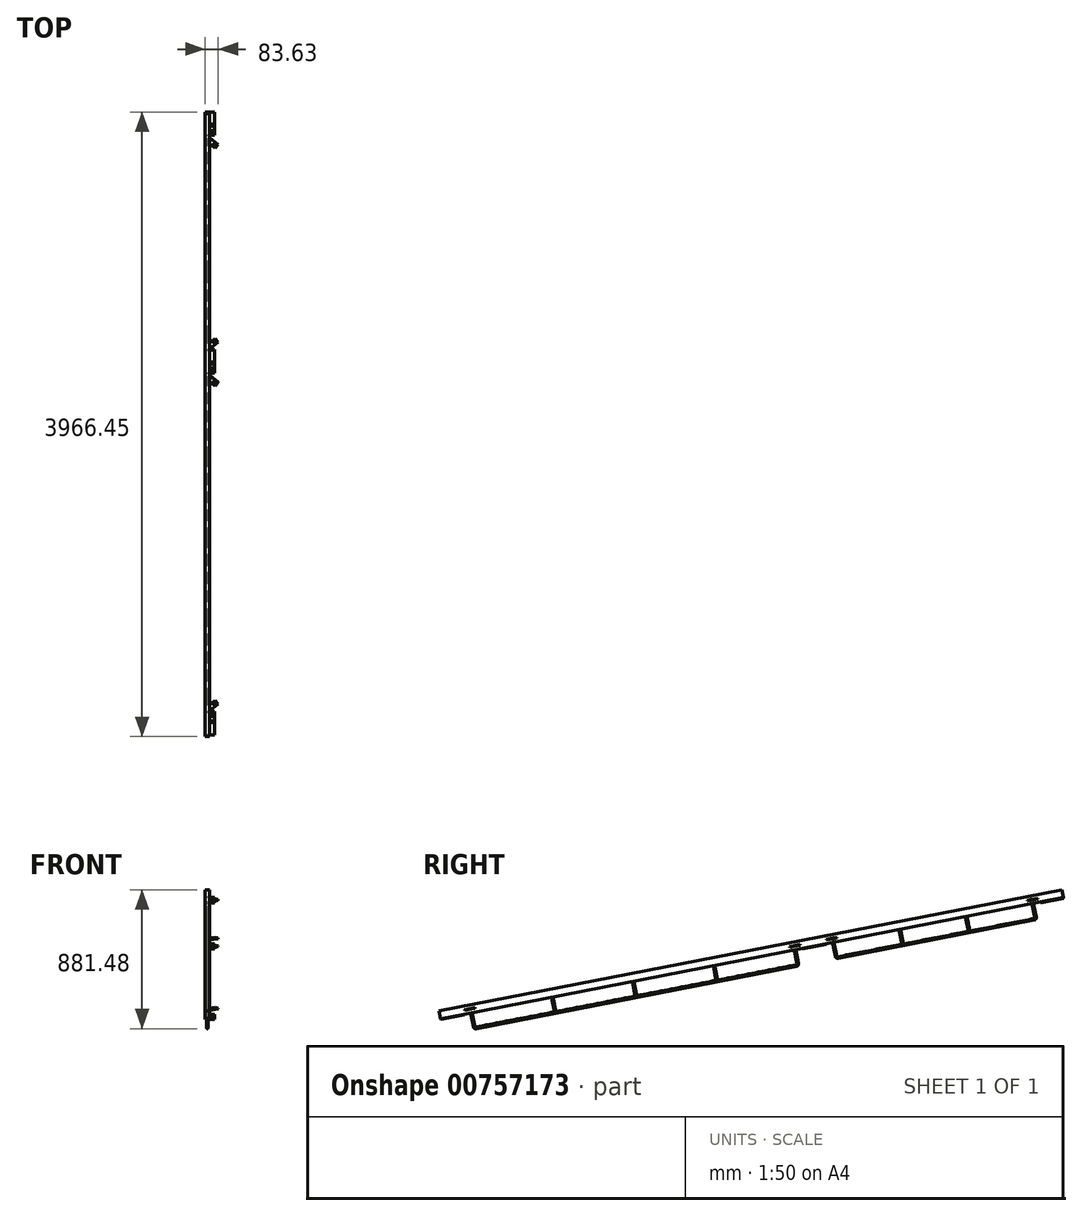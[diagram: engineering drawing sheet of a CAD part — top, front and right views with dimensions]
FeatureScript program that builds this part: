
annotation { "Feature Type Name" : "Feature", "Feature Type Description" : "" }
export const myFeature = defineFeature(function(context is Context, id is Id, definition is map)
    precondition{}
    {
        {
            var Q0;
            Q0=qCreatedBy(makeId("Top.planeOp"),FACE);
            var sketch = newSketch(context, id + "F0", { "sketchPlane" : qUnion([Q0])});
            skPoint(sketch, "E0", {"position": v(0, 0) * mm});
            skPoint(sketch, "E1", {"position": v(28.11, 0) * mm});
            skLineSegment(sketch, "E2", {"start": v(0, 0) * mm, "end": v(28.11, 0) * mm});
            skSolve(sketch);
        }
        {
            var Q0;
            Q0=qCreatedBy(makeId("Top.planeOp"),FACE);
            var Q1;
            Q1=sQuery(id+"F0.wireOp",EDGE,"E2");
            cPlane(context, id + "F1", {"entities" : qUnion([Q0, Q1]), "cplaneType" : CPlaneType.LINE_ANGLE, "offset" : 25 * mm, "angle" : 11 * degree, "width" : 150 * mm, "height" : 150 * mm});
        }
        {
            var Q0;
            Q0=qCreatedBy(id+"F1.planeOp",FACE);
            var Q1;
            Q1=sQuery(id+"F0.wireOp",EDGE,"E2");
            cPlane(context, id + "F2", {"entities" : qUnion([Q0, Q1]), "cplaneType" : CPlaneType.LINE_ANGLE, "offset" : 25 * mm, "angle" : 90 * degree, "width" : 150 * mm, "height" : 150 * mm});
        }
        {
            var Q0;
            Q0=qCreatedBy(id+"F2.planeOp",FACE);
            var sketch = newSketch(context, id + "F3", { "sketchPlane" : qUnion([Q0])});
            skLineSegment(sketch, "E3.bottom", {"start": v(15, -25) * mm, "end": v(-15, -25) * mm});
            skLineSegment(sketch, "E3.top", {"start": v(15, 25) * mm, "end": v(-15, 25) * mm});
            skLineSegment(sketch, "E3.left", {"start": v(15, -25) * mm, "end": v(15, 25) * mm});
            skLineSegment(sketch, "E3.right", {"start": v(-15, -25) * mm, "end": v(-15, 25) * mm});
            skPoint(sketch, "E3.middle", {"position": v(0, 0) * mm});
            skLineSegment(sketch, "E4.bottom", {"start": v(14, -24) * mm, "end": v(-14, -24) * mm});
            skLineSegment(sketch, "E4.top", {"start": v(14, 24) * mm, "end": v(-14, 24) * mm});
            skLineSegment(sketch, "E4.left", {"start": v(14, -24) * mm, "end": v(14, 24) * mm});
            skLineSegment(sketch, "E4.right", {"start": v(-14, -24) * mm, "end": v(-14, 24) * mm});
            skSolve(sketch);
        }
        {
            var Q0;
            Q0 = qSketchRegion(id + "F3", true);
            extrude(context, id + "F4", {"entities" : qUnion([Q0]), "depth" : 30 * mm, "offsetDistance" : 25 * mm, "hasSecondDirection" : true, "secondDirectionOppositeDirection" : true, "secondDirectionDepth" : 4000 * mm});
        }
        {
            var Q0;
            Q0=makeQuery(id+"F4.opExtrude","SWEPT_FACE",FACE,{"disambiguationData":[OSD([sQuery(id+"F3.wireOp",EDGE,"E3.bottom")])]});
            var sketch = newSketch(context, id + "F5", { "sketchPlane" : qUnion([Q0])});
            skLineSegment(sketch, "E5.0", {"start": v(45, -4000) * mm, "end": v(135, -4000) * mm});
            skLineSegment(sketch, "E6.0", {"start": v(-15, -4000) * mm, "end": v(45, -4000) * mm});
            skLineSegment(sketch, "E7.0", {"start": v(-15, -4000) * mm, "end": v(-15, -3850) * mm});
            skLineSegment(sketch, "E8.0", {"start": v(-15, -3850) * mm, "end": v(45, -3850) * mm});
            skLineSegment(sketch, "E9.0", {"start": v(45, -3940) * mm, "end": v(45, -3850) * mm});
            skLineSegment(sketch, "E10.0", {"start": v(45, -3940) * mm, "end": v(135, -3940) * mm});
            skLineSegment(sketch, "E11.0", {"start": v(135, -4000) * mm, "end": v(135, -3940) * mm});
            skCircle(sketch, "E12.0", {"center": v(70, -3955) * mm, "radius": 6 * mm});
            skCircle(sketch, "E13.0", {"center": v(110, -3955) * mm, "radius": 6 * mm});
            skCircle(sketch, "E14.0", {"center": v(30, -3915) * mm, "radius": 6 * mm});
            skCircle(sketch, "E15.0", {"center": v(30, -3875) * mm, "radius": 6 * mm});
            skLineSegment(sketch, "E16", {"start": v(45, -3940) * mm, "end": v(45, -4000) * mm});
            skSolve(sketch);
        }
        {
            var Q0;
            {var subQ0=sQuery(id+"F5.wireOp",EDGE,"E9.0");Q0=makeQuery(id+"F5.imprint","IMPRINT",FACE,{"disambiguationData":[TD([[makeQuery(id+"F5.imprint","IMPRINT",EDGE,{"derivedFrom":subQ0}),1.0]])]});}
            var Q1;
            {var subQ4=sQuery(id+"F5.wireOp",EDGE,"E7.0");Q1=makeQuery(id+"F5.imprint","IMPRINT",FACE,{"disambiguationData":[TD([[makeQuery(id+"F5.imprint","IMPRINT",EDGE,{"derivedFrom":subQ4}),1.0]])]});}
            extrude(context, id + "F6", {"entities" : qUnion([Q0, Q1]), "operationType" : NewBodyOperationType.ADD, "depth" : 5 * mm, "offsetDistance" : 25 * mm});
        }
        {
            var Q0;
            Q0=makeQuery(id+"F4.opExtrude","SWEPT_FACE",FACE,{"disambiguationData":[OSD([sQuery(id+"F3.wireOp",EDGE,"E3.bottom")])]});
            var sketch = newSketch(context, id + "F7", { "sketchPlane" : qUnion([Q0])});
            skLineSegment(sketch, "E17.0", {"start": v(45, -2401.65) * mm, "end": v(45, -2311.65) * mm});
            skLineSegment(sketch, "E18.0", {"start": v(-15, -2311.65) * mm, "end": v(45, -2311.65) * mm});
            skLineSegment(sketch, "E19.0", {"start": v(-15, -2461.65) * mm, "end": v(135, -2461.65) * mm});
            skLineSegment(sketch, "E20.0", {"start": v(135, -2461.65) * mm, "end": v(135, -2401.65) * mm});
            skLineSegment(sketch, "E21.0", {"start": v(45, -2401.65) * mm, "end": v(135, -2401.65) * mm});
            skLineSegment(sketch, "E22", {"start": v(-15, -2461.65) * mm, "end": v(-15, -2311.65) * mm});
            skLineSegment(sketch, "E23", {"start": v(45, -2401.65) * mm, "end": v(45, -2461.65) * mm});
            skCircle(sketch, "E24.0", {"center": v(30, -2376.65) * mm, "radius": 6 * mm});
            skCircle(sketch, "E25.0", {"center": v(30, -2336.65) * mm, "radius": 6 * mm});
            skSolve(sketch);
        }
        {
            var Q0;
            {var subQ0=sQuery(id+"F7.wireOp",EDGE,"E22");Q0=makeQuery(id+"F7.imprint","IMPRINT",FACE,{"disambiguationData":[TD([[makeQuery(id+"F7.imprint","IMPRINT",EDGE,{"derivedFrom":subQ0}),1.0]])]});}
            var Q1;
            {var subQ7=sQuery(id+"F7.wireOp",EDGE,"E17.0");Q1=makeQuery(id+"F7.imprint","IMPRINT",FACE,{"disambiguationData":[TD([[makeQuery(id+"F7.imprint","IMPRINT",EDGE,{"derivedFrom":subQ7}),1.0]])]});}
            extrude(context, id + "F8", {"entities" : qUnion([Q0, Q1]), "operationType" : NewBodyOperationType.ADD, "depth" : 5 * mm, "offsetDistance" : 25 * mm});
        }
        {
            var Q0;
            {var subQ3=sQuery(id+"F3.wireOp",EDGE,"E3.bottom");var subQ4=sQuery(id+"F7.wireOp",EDGE,"E18.0");Q0=makeQuery(id+"F8.boolean.opBoolean","SPLIT",FACE,{"disambiguationData":[TD([makeQuery(id+"F8.opExtrude","SWEPT_FACE",FACE,{"disambiguationData":[OSD([subQ4])]})])],"derivedFrom":makeQuery(id+"F4.opExtrude","SWEPT_FACE",FACE,{"disambiguationData":[OSD([subQ3])]})});}
            var sketch = newSketch(context, id + "F9", { "sketchPlane" : qUnion([Q0])});
            skLineSegment(sketch, "E26.0", {"start": v(-15, -120.03) * mm, "end": v(45, -120.03) * mm});
            skLineSegment(sketch, "E27.0", {"start": v(45, -30.03) * mm, "end": v(45, -120.03) * mm});
            skCircle(sketch, "E28.0", {"center": v(30, -95.03) * mm, "radius": 6 * mm});
            skCircle(sketch, "E29.0", {"center": v(30, -55.03) * mm, "radius": 6 * mm});
            skLineSegment(sketch, "E30.0", {"start": v(45, -30.03) * mm, "end": v(135, -30.03) * mm});
            skLineSegment(sketch, "E31.0", {"start": v(-15, 29) * mm, "end": v(135, 29) * mm});
            skLineSegment(sketch, "E32", {"start": v(-15, -120.03) * mm, "end": v(-15, 29) * mm});
            skLineSegment(sketch, "E33", {"start": v(45, -30.03) * mm, "end": v(45, 30) * mm});
            skSolve(sketch);
        }
        {
            var Q0;
            Q0 = qSketchRegion(id + "F9", true);
            extrude(context, id + "F10", {"entities" : qUnion([Q0]), "operationType" : NewBodyOperationType.ADD, "depth" : 4.8 * mm, "offsetDistance" : 25 * mm});
        }
        {
            var Q0;
            Q0=qCreatedBy(id+"F1.planeOp",FACE);
            var sketch = newSketch(context, id + "F11", { "sketchPlane" : qUnion([Q0])});
            skLineSegment(sketch, "E34.0", {"start": v(15, -3850) * mm, "end": v(45, -3850) * mm});
            skLineSegment(sketch, "E35", {"start": v(15, -3850) * mm, "end": v(15, -3840) * mm});
            skLineSegment(sketch, "E36", {"start": v(41, -1985.01) * mm, "end": v(15.07, -1985.01) * mm});
            skLineSegment(sketch, "E37.MirrorCS", {"start": v(15, -3840) * mm, "end": v(68.63, -3795) * mm});
            skLineSegment(sketch, "E38.MirrorCS", {"start": v(68.63, -3795) * mm, "end": v(49.34, -3772.03) * mm});
            skLineSegment(sketch, "E39.MirrorCS", {"start": v(49.34, -3772.03) * mm, "end": v(14.87, -3800.95) * mm});
            skCircle(sketch, "E40.MirrorC", {"center": v(43.27, -3796.7) * mm, "radius": 6 * mm});
            skLineSegment(sketch, "E41.MirrorCS", {"start": v(43.27, -3796.7) * mm, "end": v(58.99, -3783.52) * mm, "construction": true});
            skLineSegment(sketch, "E42", {"start": v(15, -3840) * mm, "end": v(14.87, -3800.95) * mm});
            skLineSegment(sketch, "E43.MirrorCS", {"start": v(15, -130.03) * mm, "end": v(68.63, -175.02) * mm});
            skCircle(sketch, "E44.MirrorC", {"center": v(43.27, -173.32) * mm, "radius": 6 * mm});
            skLineSegment(sketch, "E45.MirrorCS", {"start": v(43.27, -173.32) * mm, "end": v(58.99, -186.5) * mm, "construction": true});
            skLineSegment(sketch, "E46.MirrorCS", {"start": v(68.63, -175.02) * mm, "end": v(49.34, -198) * mm});
            skLineSegment(sketch, "E47.MirrorCS", {"start": v(49.34, -198) * mm, "end": v(14.87, -169.08) * mm});
            skLineSegment(sketch, "E48.MirrorCS", {"start": v(15, -130.03) * mm, "end": v(14.87, -169.08) * mm});
            skPoint(sketch, "E49.0", {"position": v(30, -2311.65) * mm});
            skLineSegment(sketch, "E50.0", {"start": v(15, -2311.65) * mm, "end": v(45, -2311.65) * mm});
            skLineSegment(sketch, "E51.0", {"start": v(15, -2461.65) * mm, "end": v(45, -2461.65) * mm});
            skLineSegment(sketch, "E52", {"start": v(15, -2311.65) * mm, "end": v(15, -2301.65) * mm});
            skLineSegment(sketch, "E53", {"start": v(15, -2461.65) * mm, "end": v(15, -2471.65) * mm});
            skLineSegment(sketch, "E54", {"start": v(15, -2301.65) * mm, "end": v(15, -130.03) * mm});
            skLineSegment(sketch, "E55", {"start": v(45.74, -1215.84) * mm, "end": v(15, -1215.84) * mm});
            skLineSegment(sketch, "E56.MirrorCS", {"start": v(49.34, -2233.67) * mm, "end": v(14.87, -2262.6) * mm});
            skLineSegment(sketch, "E57.MirrorCS", {"start": v(15, -2301.65) * mm, "end": v(14.87, -2262.6) * mm});
            skLineSegment(sketch, "E58.MirrorCS", {"start": v(15, -2301.65) * mm, "end": v(68.63, -2256.65) * mm});
            skLineSegment(sketch, "E59.MirrorCS", {"start": v(68.63, -2256.65) * mm, "end": v(49.34, -2233.67) * mm});
            skLineSegment(sketch, "E60.MirrorCS", {"start": v(43.27, -2258.35) * mm, "end": v(58.99, -2245.16) * mm, "construction": true});
            skCircle(sketch, "E61.MirrorC", {"center": v(43.27, -2258.35) * mm, "radius": 6 * mm});
            skLineSegment(sketch, "E62", {"start": v(15, -2471.65) * mm, "end": v(15, -3840) * mm});
            skLineSegment(sketch, "E63", {"start": v(29.54, -3155.82) * mm, "end": v(15, -3155.82) * mm});
            skLineSegment(sketch, "E64.MirrorCS", {"start": v(15, -2471.65) * mm, "end": v(68.63, -2516.64) * mm});
            skLineSegment(sketch, "E65.MirrorCS", {"start": v(15, -2471.65) * mm, "end": v(14.87, -2510.7) * mm});
            skLineSegment(sketch, "E66.MirrorCS", {"start": v(49.34, -2539.62) * mm, "end": v(14.87, -2510.7) * mm});
            skLineSegment(sketch, "E67.MirrorCS", {"start": v(68.63, -2516.64) * mm, "end": v(49.34, -2539.62) * mm});
            skCircle(sketch, "E68.MirrorC", {"center": v(43.27, -2514.94) * mm, "radius": 6 * mm});
            skLineSegment(sketch, "E69.MirrorCS", {"start": v(43.27, -2514.94) * mm, "end": v(58.99, -2528.13) * mm, "construction": true});
            skLineSegment(sketch, "E70.0", {"start": v(16.29, -2303.18) * mm, "end": v(69.91, -2258.19) * mm});
            skLineSegment(sketch, "E71.0", {"start": v(48.06, -2232.14) * mm, "end": v(13.58, -2261.06) * mm});
            skLineSegment(sketch, "E72.0", {"start": v(16.29, -2470.11) * mm, "end": v(69.91, -2515.1) * mm});
            skLineSegment(sketch, "E73.0", {"start": v(48.06, -2541.15) * mm, "end": v(13.58, -2512.23) * mm});
            skLineSegment(sketch, "E74.0", {"start": v(16.29, -3841.53) * mm, "end": v(69.91, -3796.54) * mm});
            skLineSegment(sketch, "E75.0", {"start": v(48.06, -3770.5) * mm, "end": v(13.58, -3799.42) * mm});
            skLineSegment(sketch, "E76.0", {"start": v(16.29, -128.5) * mm, "end": v(69.91, -173.48) * mm});
            skLineSegment(sketch, "E77.0", {"start": v(48.06, -199.53) * mm, "end": v(13.58, -170.6) * mm});
            skSolve(sketch);
        }
        {
            var Q0;
            Q0 = qSketchRegion(id + "F11", true);
            extrude(context, id + "F12", {"entities" : qUnion([Q0]), "operationType" : NewBodyOperationType.ADD, "depth" : 2.5 * mm, "offsetDistance" : 25 * mm, "hasSecondDirection" : true, "secondDirectionOppositeDirection" : true, "secondDirectionDepth" : 2.5 * mm});
        }
        {
            var Q0;
            Q0=qCreatedBy(makeId("Right.planeOp"),FACE);
            var sketch = newSketch(context, id + "F13", { "sketchPlane" : qUnion([Q0])});
            skLineSegment(sketch, "E78", {"start": v(166.55, 29.83) * mm, "end": v(170.85, 7.74) * mm});
            skLineSegment(sketch, "E79", {"start": v(170.85, 7.74) * mm, "end": v(188.02, -80.6) * mm});
            skLineSegment(sketch, "E80", {"start": v(188.02, -80.6) * mm, "end": v(197.84, -78.7) * mm});
            skArc(sketch, "E81", {"start": v(188.02, -80.6) * mm, "mid": v(192.24, -86.99) * mm, "end": v(199.74, -88.51) * mm});
            skLineSegment(sketch, "E82", {"start": v(197.84, -78.7) * mm, "end": v(199.74, -88.51) * mm, "construction": true});
            skPoint(sketch, "E83.0", {"position": v(166.55, 29.83) * mm});
            skPoint(sketch, "E84.0", {"position": v(165.6, 34.74) * mm});
            skLineSegment(sketch, "E85", {"start": v(165.6, 34.74) * mm, "end": v(166.55, 29.83) * mm});
            skPoint(sketch, "E86.0", {"position": v(2221.4, 429.25) * mm});
            skPoint(sketch, "E87.0", {"position": v(2220.44, 434.16) * mm});
            skLineSegment(sketch, "E88", {"start": v(2220.44, 434.16) * mm, "end": v(2221.4, 429.25) * mm});
            skLineSegment(sketch, "E89", {"start": v(2221.4, 429.25) * mm, "end": v(2225.69, 407.16) * mm});
            skLineSegment(sketch, "E90", {"start": v(2225.69, 407.16) * mm, "end": v(2242.86, 318.82) * mm});
            skLineSegment(sketch, "E91", {"start": v(2242.86, 318.82) * mm, "end": v(2233.04, 316.9) * mm, "construction": true});
            skArc(sketch, "E92", {"start": v(2234.95, 307.1) * mm, "mid": v(2241.33, 311.32) * mm, "end": v(2242.86, 318.82) * mm});
            skLineSegment(sketch, "E93", {"start": v(2233.04, 316.9) * mm, "end": v(2234.95, 307.1) * mm});
            skLineSegment(sketch, "E94", {"start": v(1217.35, 109.29) * mm, "end": v(1198.27, 207.45) * mm});
            skLineSegment(sketch, "E95", {"start": v(1731.06, 209.14) * mm, "end": v(1711.98, 307.3) * mm});
            skLineSegment(sketch, "E96", {"start": v(703.64, 9.43) * mm, "end": v(684.56, 107.6) * mm});
            skLineSegment(sketch, "E97", {"start": v(199.74, -88.51) * mm, "end": v(2234.95, 307.1) * mm});
            skPoint(sketch, "E98.0", {"position": v(2465.15, 476.63) * mm});
            skPoint(sketch, "E99.0", {"position": v(2464.2, 481.54) * mm});
            skPoint(sketch, "E100.0", {"position": v(3730.53, 727.69) * mm});
            skPoint(sketch, "E101.0", {"position": v(3731.49, 722.78) * mm});
            skLineSegment(sketch, "E102", {"start": v(3730.53, 727.69) * mm, "end": v(3731.49, 722.78) * mm});
            skLineSegment(sketch, "E103", {"start": v(2465.15, 476.63) * mm, "end": v(2464.2, 481.54) * mm});
            skLineSegment(sketch, "E104", {"start": v(2465.15, 476.63) * mm, "end": v(2469.44, 454.54) * mm});
            skLineSegment(sketch, "E105", {"start": v(3731.49, 722.78) * mm, "end": v(3735.78, 700.7) * mm});
            skLineSegment(sketch, "E106", {"start": v(3735.78, 700.7) * mm, "end": v(3752.95, 612.35) * mm});
            skLineSegment(sketch, "E107", {"start": v(3752.95, 612.35) * mm, "end": v(3743.13, 610.44) * mm});
            skArc(sketch, "E108", {"start": v(3745.04, 600.62) * mm, "mid": v(3751.43, 604.85) * mm, "end": v(3752.95, 612.35) * mm});
            skLineSegment(sketch, "E109", {"start": v(3743.13, 610.44) * mm, "end": v(3745.04, 600.62) * mm, "construction": true});
            skLineSegment(sketch, "E110", {"start": v(2469.44, 454.54) * mm, "end": v(2486.62, 366.2) * mm});
            skLineSegment(sketch, "E111", {"start": v(2486.62, 366.2) * mm, "end": v(2496.43, 368.1) * mm});
            skArc(sketch, "E112", {"start": v(2486.62, 366.2) * mm, "mid": v(2490.97, 359.73) * mm, "end": v(2498.64, 358.35) * mm});
            skLineSegment(sketch, "E113", {"start": v(2496.43, 368.1) * mm, "end": v(2498.34, 358.29) * mm, "construction": true});
            skLineSegment(sketch, "E114", {"start": v(2469.44, 454.54) * mm, "end": v(2891.56, 536.6) * mm, "construction": true});
            skLineSegment(sketch, "E115", {"start": v(2891.56, 536.6) * mm, "end": v(3313.67, 618.64) * mm, "construction": true});
            skLineSegment(sketch, "E116", {"start": v(3313.67, 618.64) * mm, "end": v(3333.52, 520.63) * mm});
            skLineSegment(sketch, "E117", {"start": v(2891.56, 536.6) * mm, "end": v(2911.41, 438.58) * mm});
            skLineSegment(sketch, "E118", {"start": v(3313.67, 618.64) * mm, "end": v(3735.78, 700.7) * mm, "construction": true});
            skLineSegment(sketch, "E119", {"start": v(170.85, 7.74) * mm, "end": v(684.56, 107.6) * mm, "construction": true});
            skLineSegment(sketch, "E120", {"start": v(1198.27, 207.45) * mm, "end": v(684.56, 107.6) * mm, "construction": true});
            skLineSegment(sketch, "E121", {"start": v(1198.27, 207.45) * mm, "end": v(1711.98, 307.3) * mm, "construction": true});
            skLineSegment(sketch, "E122", {"start": v(1711.98, 307.3) * mm, "end": v(2225.69, 407.16) * mm, "construction": true});
            skLineSegment(sketch, "E123", {"start": v(2498.64, 358.35) * mm, "end": v(3745.04, 600.62) * mm});
            skSolve(sketch);
        }
        {
            var Q0;
            {var subQ7=sQuery(id+"F7.wireOp",EDGE,"E18.0");var subQ9=makeQuery(id+"F8.opExtrude","SWEPT_FACE",FACE,{"disambiguationData":[OSD([subQ7])]});var subQ12=sQuery(id+"F3.wireOp",EDGE,"E3.bottom");Q0=makeQuery(id+"F10.boolean.opBoolean","SPLIT",FACE,{"disambiguationData":[TD([subQ9])],"derivedFrom":makeQuery(id+"F8.boolean.opBoolean","SPLIT",FACE,{"disambiguationData":[TD([subQ9])],"derivedFrom":makeQuery(id+"F4.opExtrude","SWEPT_FACE",FACE,{"disambiguationData":[OSD([subQ12])]})})});}
            var sketch = newSketch(context, id + "F14", { "sketchPlane" : qUnion([Q0])});
            skCircle(sketch, "E124", {"center": v(0, -169.19) * mm, "radius": 5 * mm});
            skCircle(sketch, "E125", {"center": v(0, -692.51) * mm, "radius": 5 * mm});
            skCircle(sketch, "E126", {"center": v(0, -1215.84) * mm, "radius": 5 * mm});
            skCircle(sketch, "E127", {"center": v(0, -1739.16) * mm, "radius": 5 * mm});
            skCircle(sketch, "E128", {"center": v(0, -2262.49) * mm, "radius": 5 * mm});
            skCircle(sketch, "E129", {"center": v(0, -2510.8) * mm, "radius": 5 * mm});
            skCircle(sketch, "E130", {"center": v(0, -2940.82) * mm, "radius": 5 * mm});
            skCircle(sketch, "E131", {"center": v(0, -3370.83) * mm, "radius": 5 * mm});
            skCircle(sketch, "E132", {"center": v(0, -3800.84) * mm, "radius": 5 * mm});
            skSolve(sketch);
        }
        {
            var Q0;
            Q0=makeQuery(id+"F14.imprint","IMPRINT",FACE,{"disambiguationData":[TD([[makeQuery(id+"F14.imprint","IMPRINT",EDGE,{"derivedFrom":sQuery(id+"F14.wireOp",EDGE,"E124")}),1.0]])]});
            var Q1;
            Q1=sQuery(id+"F13.wireOp",EDGE,"E79");
            var Q2;
            Q2=sQuery(id+"F13.wireOp",EDGE,"E81");
            var Q3;
            Q3=sQuery(id+"F13.wireOp",EDGE,"E97");
            var Q4;
            Q4=sQuery(id+"F13.wireOp",EDGE,"E92");
            var Q5;
            Q5=sQuery(id+"F13.wireOp",EDGE,"E90");
            sweep(context, id + "F15", {"operationType" : NewBodyOperationType.ADD, "profiles" : qUnion([Q0]), "path" : qUnion([Q1, Q2, Q3, Q4, Q5])});
        }
        {
            var Q0;
            Q0=makeQuery(id+"F14.imprint","IMPRINT",FACE,{"disambiguationData":[TD([[makeQuery(id+"F14.imprint","IMPRINT",EDGE,{"derivedFrom":sQuery(id+"F14.wireOp",EDGE,"E125")}),1.0]])]});
            var Q1;
            Q1=sQuery(id+"F13.wireOp",EDGE,"E96");
            sweep(context, id + "F16", {"operationType" : NewBodyOperationType.ADD, "profiles" : qUnion([Q0]), "path" : qUnion([Q1])});
        }
        {
            var Q0;
            Q0=makeQuery(id+"F14.imprint","IMPRINT",FACE,{"disambiguationData":[TD([[makeQuery(id+"F14.imprint","IMPRINT",EDGE,{"derivedFrom":sQuery(id+"F14.wireOp",EDGE,"E126")}),1.0]])]});
            var Q1;
            Q1=sQuery(id+"F13.wireOp",EDGE,"E94");
            sweep(context, id + "F17", {"operationType" : NewBodyOperationType.ADD, "profiles" : qUnion([Q0]), "path" : qUnion([Q1])});
        }
        {
            var Q0;
            Q0=makeQuery(id+"F14.imprint","IMPRINT",FACE,{"disambiguationData":[TD([[makeQuery(id+"F14.imprint","IMPRINT",EDGE,{"derivedFrom":sQuery(id+"F14.wireOp",EDGE,"E127")}),1.0]])]});
            var Q1;
            Q1=sQuery(id+"F13.wireOp",EDGE,"E95");
            sweep(context, id + "F18", {"operationType" : NewBodyOperationType.ADD, "profiles" : qUnion([Q0]), "path" : qUnion([Q1])});
        }
        {
            var Q0;
            Q0=makeQuery(id+"F14.imprint","IMPRINT",FACE,{"disambiguationData":[TD([[makeQuery(id+"F14.imprint","IMPRINT",EDGE,{"derivedFrom":sQuery(id+"F14.wireOp",EDGE,"E129")}),1.0]])]});
            var Q1;
            Q1=sQuery(id+"F13.wireOp",EDGE,"E110");
            var Q2;
            Q2=sQuery(id+"F13.wireOp",EDGE,"E112");
            var Q3;
            Q3=sQuery(id+"F13.wireOp",EDGE,"E123");
            var Q4;
            Q4=sQuery(id+"F13.wireOp",EDGE,"E108");
            var Q5;
            Q5=sQuery(id+"F13.wireOp",EDGE,"E106");
            sweep(context, id + "F19", {"operationType" : NewBodyOperationType.ADD, "profiles" : qUnion([Q0]), "path" : qUnion([Q1, Q2, Q3, Q4, Q5])});
        }
        {
            var Q0;
            Q0=makeQuery(id+"F14.imprint","IMPRINT",FACE,{"disambiguationData":[TD([[makeQuery(id+"F14.imprint","IMPRINT",EDGE,{"derivedFrom":sQuery(id+"F14.wireOp",EDGE,"E130")}),1.0]])]});
            var Q1;
            Q1=sQuery(id+"F13.wireOp",EDGE,"E117");
            sweep(context, id + "F20", {"operationType" : NewBodyOperationType.ADD, "profiles" : qUnion([Q0]), "path" : qUnion([Q1])});
        }
        {
            var Q0;
            Q0=makeQuery(id+"F14.imprint","IMPRINT",FACE,{"disambiguationData":[TD([[makeQuery(id+"F14.imprint","IMPRINT",EDGE,{"derivedFrom":sQuery(id+"F14.wireOp",EDGE,"E131")}),1.0]])]});
            var Q1;
            Q1=sQuery(id+"F13.wireOp",EDGE,"E116");
            sweep(context, id + "F21", {"operationType" : NewBodyOperationType.ADD, "profiles" : qUnion([Q0]), "path" : qUnion([Q1])});
        }
    });
